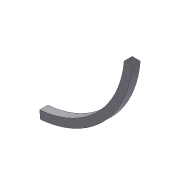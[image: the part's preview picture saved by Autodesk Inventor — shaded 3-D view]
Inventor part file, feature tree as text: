
AUTODESK INVENTOR PART (.ipt)
format: ipt  version: 2012 (Build 160160000, 160)  size: 87,552 bytes
history: native  units: in
note: dims shown in document units (in); Inventor stores cm internally (conversion verified against a paired STEP export)
features: extrude x1, shell x1, sketch x1
ambient origin geometry x8: Origin, YZ Plane, XZ Plane, XY Plane, X Axis, Y Axis, Z Axis, Center Point
bodies: Solid1 (feature_tree)
feature tree (3):
  extrude  "Extrusion1"  Depth=1.0in
  shell  "Shell1"  Thickness=1.0in
  sketch  "Sketch1"  dims[d0=11.5in d1=1.0in d5=1.0in d6=0.0in d7=0.0625in d9=1.0in d10=0.5497in]
